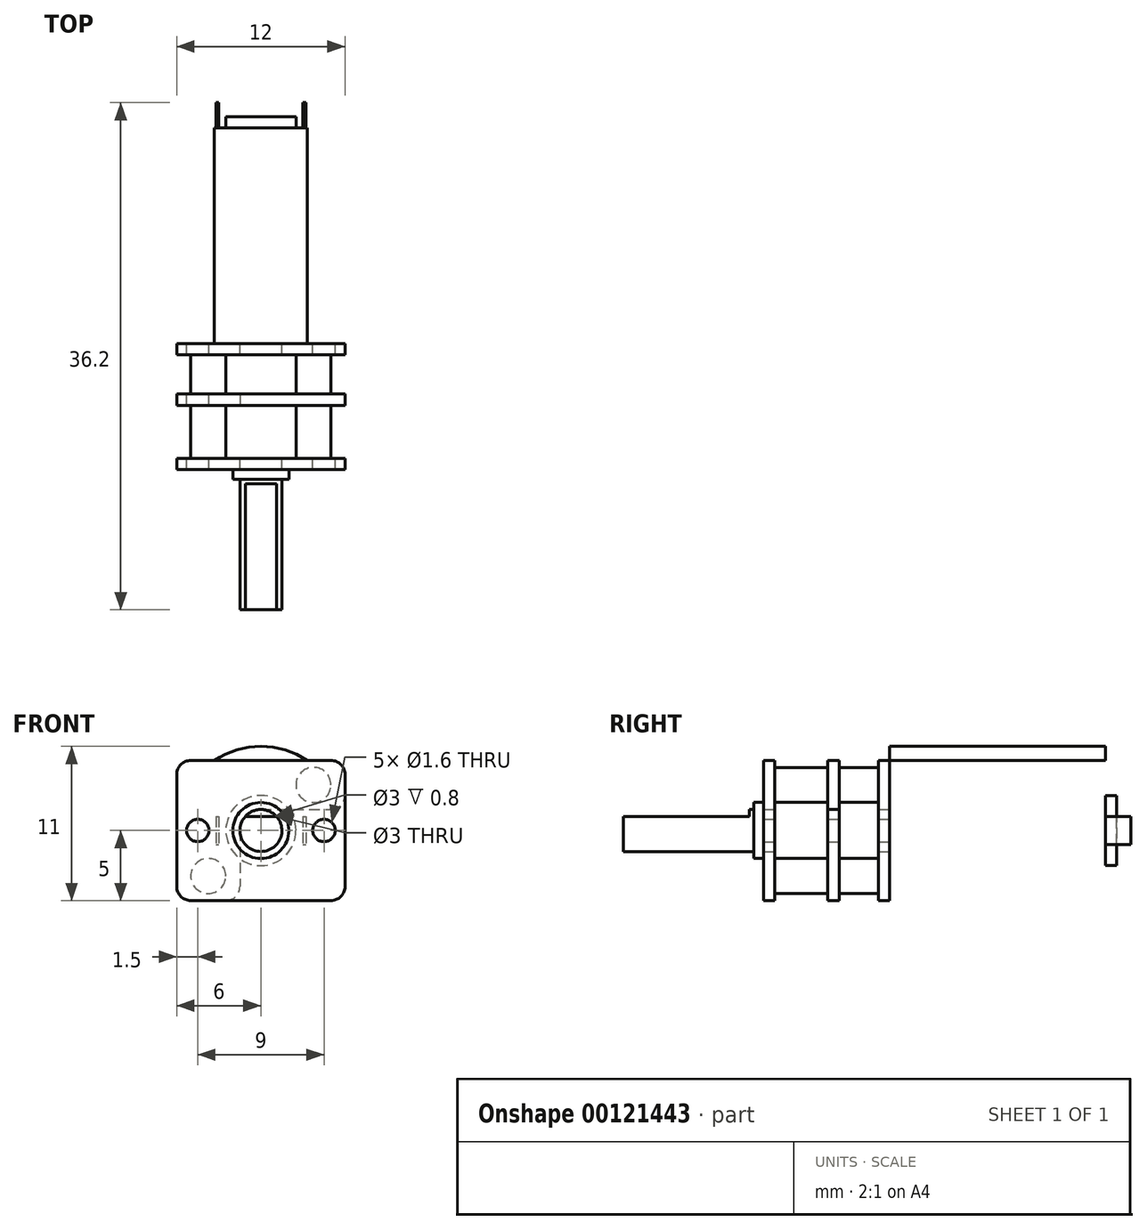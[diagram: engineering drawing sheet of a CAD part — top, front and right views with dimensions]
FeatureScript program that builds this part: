
annotation { "Feature Type Name" : "Feature", "Feature Type Description" : "" }
export const myFeature = defineFeature(function(context is Context, id is Id, definition is map)
    precondition{}
    {
        {
            var Q0;
            Q0=qCreatedBy(makeId("Front.planeOp"),FACE);
            var sketch = newSketch(context, id + "F0", { "sketchPlane" : qUnion([Q0])});
            skCircle(sketch, "E0", {"center": v(0, 0) * mm, "radius": 6 * mm});
            skLineSegment(sketch, "E1.bottom", {"start": v(-6, -5) * mm, "end": v(6, -5) * mm});
            skLineSegment(sketch, "E1.top", {"start": v(-6, 5) * mm, "end": v(6, 5) * mm});
            skLineSegment(sketch, "E1.left", {"start": v(-6, -5) * mm, "end": v(-6, 5) * mm});
            skLineSegment(sketch, "E1.right", {"start": v(6, -5) * mm, "end": v(6, 5) * mm});
            skSolve(sketch);
        }
        {
            var Q0;
            {var subQ0=sQuery(id+"F0.wireOp",EDGE,"E0");var subQ6=sQuery(id+"F0.wireOp",EDGE,"E1.top");var subQ7=makeQuery(id+"F0.imprint","INTERSECT",VERTEX,{"disambiguationData":[OD(0.0)],"derivedFrom":[subQ0,subQ6]});Q0=makeQuery(id+"F0.imprint","IMPRINT",FACE,{"disambiguationData":[TD([[makeQuery(id+"F0.imprint","IMPRINT",EDGE,{"disambiguationData":[TD([[subQ7,1.0]])],"derivedFrom":subQ0}),1.0]])]});}
            extrude(context, id + "F1", {"entities" : qUnion([Q0]), "depth" : 15.4 * mm});
        }
        {
            var Q0;
            Q0=qCreatedBy(makeId("Front.planeOp"),FACE);
            var sketch = newSketch(context, id + "F2", { "sketchPlane" : qUnion([Q0])});
            skLineSegment(sketch, "E2.bottom", {"start": v(-3.2, 1) * mm, "end": v(-3, 1) * mm});
            skLineSegment(sketch, "E2.top", {"start": v(-3.2, -1) * mm, "end": v(-3, -1) * mm});
            skLineSegment(sketch, "E2.left", {"start": v(-3.2, 1) * mm, "end": v(-3.2, -1) * mm});
            skLineSegment(sketch, "E2.right", {"start": v(-3, 1) * mm, "end": v(-3, -1) * mm});
            skLineSegment(sketch, "E3.bottom", {"start": v(3, 1) * mm, "end": v(3.2, 1) * mm});
            skLineSegment(sketch, "E3.top", {"start": v(3, -1) * mm, "end": v(3.2, -1) * mm});
            skLineSegment(sketch, "E3.left", {"start": v(3, 1) * mm, "end": v(3, -1) * mm});
            skLineSegment(sketch, "E3.right", {"start": v(3.2, 1) * mm, "end": v(3.2, -1) * mm});
            skLineSegment(sketch, "E4", {"start": v(-3, 0) * mm, "end": v(3, 0) * mm});
            skCircle(sketch, "E5", {"center": v(0, 0) * mm, "radius": 2.5 * mm});
            skSolve(sketch);
        }
        {
            var Q0;
            {var subQ0=sQuery(id+"F2.wireOp",EDGE,"E5");var subQ1=sQuery(id+"F2.wireOp",EDGE,"E4");var subQ2=makeQuery(id+"F2.imprint","INTERSECT",VERTEX,{"disambiguationData":[OD(0.0)],"derivedFrom":[subQ1,subQ0]});Q0=makeQuery(id+"F2.imprint","IMPRINT",FACE,{"disambiguationData":[TD([[makeQuery(id+"F2.imprint","IMPRINT",EDGE,{"disambiguationData":[TD([[subQ2,-1.0]])],"derivedFrom":subQ1}),-1.0]])]});}
            var Q1;
            {var subQ0=sQuery(id+"F2.wireOp",EDGE,"E5");var subQ1=sQuery(id+"F2.wireOp",EDGE,"E4");var subQ2=makeQuery(id+"F2.imprint","INTERSECT",VERTEX,{"disambiguationData":[OD(0.0)],"derivedFrom":[subQ1,subQ0]});Q1=makeQuery(id+"F2.imprint","IMPRINT",FACE,{"disambiguationData":[TD([[makeQuery(id+"F2.imprint","IMPRINT",EDGE,{"disambiguationData":[TD([[subQ2,-1.0]])],"derivedFrom":subQ1}),1.0]])]});}
            extrude(context, id + "F3", {"entities" : qUnion([Q0, Q1]), "operationType" : NewBodyOperationType.ADD, "oppositeDirection" : true, "depth" : .8 * mm});
        }
        {
            var Q0;
            {var subQ3=sQuery(id+"F2.wireOp",EDGE,"E3.bottom");Q0=makeQuery(id+"F2.imprint","IMPRINT",FACE,{"disambiguationData":[TD([[makeQuery(id+"F2.imprint","IMPRINT",EDGE,{"derivedFrom":subQ3}),-1.0]])]});}
            var Q1;
            {var subQ1=sQuery(id+"F2.wireOp",EDGE,"E2.bottom");Q1=makeQuery(id+"F2.imprint","IMPRINT",FACE,{"disambiguationData":[TD([[makeQuery(id+"F2.imprint","IMPRINT",EDGE,{"derivedFrom":subQ1}),-1.0]])]});}
            extrude(context, id + "F4", {"entities" : qUnion([Q0, Q1]), "operationType" : NewBodyOperationType.ADD, "oppositeDirection" : true, "depth" : 1.8 * mm});
        }
        {
            var Q0;
            Q0=makeQuery(id+"F1.opExtrude","CAP_FACE",FACE,{"disambiguationData":[OSD([sQuery(id+"F0.wireOp",EDGE,"E0"),sQuery(id+"F0.wireOp",EDGE,"E1.bottom"),sQuery(id+"F0.wireOp",EDGE,"E1.top")])],"isStart":false});
            var sketch = newSketch(context, id + "F5", { "sketchPlane" : qUnion([Q0])});
            skLineSegment(sketch, "E6.bottom", {"start": v(-5, 5) * mm, "end": v(5, 5) * mm});
            skLineSegment(sketch, "E6.top", {"start": v(-5, -5) * mm, "end": v(5, -5) * mm});
            skLineSegment(sketch, "E6.left", {"start": v(-6, 4) * mm, "end": v(-6, -4) * mm});
            skLineSegment(sketch, "E6.right", {"start": v(6, 4) * mm, "end": v(6, -4) * mm});
            skPoint(sketch, "E7.visualSharp", {"position": v(-6, 5) * mm});
            skArc(sketch, "E7.filletArc", {"start": v(-5, 5) * mm, "mid": v(-5.7, 4.7) * mm, "end": v(-6, 4) * mm});
            skPoint(sketch, "E8.visualSharp", {"position": v(6, 5) * mm});
            skArc(sketch, "E8.filletArc", {"start": v(6, 4) * mm, "mid": v(5.7, 4.7) * mm, "end": v(5, 5) * mm});
            skPoint(sketch, "E9.visualSharp", {"position": v(6, -5) * mm});
            skArc(sketch, "E9.filletArc", {"start": v(5, -5) * mm, "mid": v(5.7, -4.7) * mm, "end": v(6, -4) * mm});
            skPoint(sketch, "E10.visualSharp", {"position": v(-6, -5) * mm});
            skArc(sketch, "E10.filletArc", {"start": v(-6, -4) * mm, "mid": v(-5.7, -4.7) * mm, "end": v(-5, -5) * mm});
            skCircle(sketch, "E11", {"center": v(-4.5, 0) * mm, "radius": 0.8 * mm});
            skCircle(sketch, "E12", {"center": v(4.5, 0) * mm, "radius": 0.8 * mm});
            skCircle(sketch, "E13", {"center": v(0, 0) * mm, "radius": 1.5 * mm});
            skSolve(sketch);
        }
        {
            var Q0;
            Q0 = qSketchRegion(id + "F5", true);
            extrude(context, id + "F6", {"entities" : qUnion([Q0]), "operationType" : NewBodyOperationType.ADD, "depth" : 9 * mm});
        }
        {
            var Q0;
            Q0=qCreatedBy(makeId("Right.planeOp"),FACE);
            var sketch = newSketch(context, id + "F7", { "sketchPlane" : qUnion([Q0])});
            skLineSegment(sketch, "E14.bottom", {"start": v(-23.6, 5) * mm, "end": v(-19.8, 5) * mm});
            skLineSegment(sketch, "E14.top", {"start": v(-23.6, -5) * mm, "end": v(-19.8, -5) * mm});
            skLineSegment(sketch, "E14.left", {"start": v(-23.6, 5) * mm, "end": v(-23.6, -5) * mm});
            skLineSegment(sketch, "E14.right", {"start": v(-19.8, 5) * mm, "end": v(-19.8, -5) * mm});
            skLineSegment(sketch, "E15.bottom", {"start": v(-19, 5) * mm, "end": v(-16.2, 5) * mm});
            skLineSegment(sketch, "E15.top", {"start": v(-19, -5) * mm, "end": v(-16.2, -5) * mm});
            skLineSegment(sketch, "E15.left", {"start": v(-19, 5) * mm, "end": v(-19, -5) * mm});
            skLineSegment(sketch, "E15.right", {"start": v(-16.2, 5) * mm, "end": v(-16.2, -5) * mm});
            skSolve(sketch);
        }
        {
            var Q0;
            Q0 = qSketchRegion(id + "F7", true);
            extrude(context, id + "F8", {"entities" : qUnion([Q0]), "operationType" : NewBodyOperationType.REMOVE, "oppositeDirection" : true, "depth" : 25 * mm, "hasSecondDirection" : true, "secondDirectionOppositeDirection" : false, "secondDirectionDepth" : 25 * mm});
        }
        {
            var Q0;
            Q0=makeQuery(id+"F8.boolean.opBoolean","COPY",FACE,{"derivedFrom":makeQuery(id+"F8.opExtrude","SWEPT_FACE",FACE,{"disambiguationData":[OSD([sQuery(id+"F7.wireOp",EDGE,"E14.right")])]})});
            var sketch = newSketch(context, id + "F9", { "sketchPlane" : qUnion([Q0])});
            skPoint(sketch, "E16.visualSharp", {"position": v(6, 0) * mm});
            skPoint(sketch, "E17.visualSharp", {"position": v(0, -5) * mm});
            skLineSegment(sketch, "E18", {"start": v(0, 1.5) * mm, "end": v(5, 1.5) * mm});
            skLineSegment(sketch, "E19", {"start": v(-1.5, 0) * mm, "end": v(-1.5, -4) * mm});
            skLineSegment(sketch, "E20", {"start": v(-1.5, -6) * mm, "end": v(7, -6) * mm});
            skArc(sketch, "E21", {"start": v(0, 1.5) * mm, "mid": v(-1.06, 1.06) * mm, "end": v(-1.5, 0) * mm});
            skLineSegment(sketch, "E22", {"start": v(6, 2.5) * mm, "end": v(6, 2.5) * mm});
            skLineSegment(sketch, "E23", {"start": v(6, 2.5) * mm, "end": v(7, 2.5) * mm});
            skLineSegment(sketch, "E24", {"start": v(-2.5, -5) * mm, "end": v(-2.5, -5) * mm});
            skLineSegment(sketch, "E25", {"start": v(-2.5, -5) * mm, "end": v(-2.5, -6) * mm});
            skLineSegment(sketch, "E26", {"start": v(-2.5, -6) * mm, "end": v(-1.5, -6) * mm});
            skLineSegment(sketch, "E27", {"start": v(7, 2.5) * mm, "end": v(7, -6) * mm});
            skPoint(sketch, "E28.visualSharp", {"position": v(6, 1.5) * mm});
            skArc(sketch, "E28.filletArc", {"start": v(5, 1.5) * mm, "mid": v(5.7, 1.8) * mm, "end": v(6, 2.5) * mm});
            skPoint(sketch, "E29.visualSharp", {"position": v(-1.5, -5) * mm});
            skArc(sketch, "E29.filletArc", {"start": v(-2.5, -5) * mm, "mid": v(-1.8, -4.7) * mm, "end": v(-1.5, -4) * mm});
            skSolve(sketch);
        }
        {
            var Q0;
            Q0 = qSketchRegion(id + "F9", true);
            extrude(context, id + "F10", {"entities" : qUnion([Q0]), "operationType" : NewBodyOperationType.REMOVE, "oppositeDirection" : true, "depth" : 1 * mm});
        }
        {
            var Q0;
            Q0=makeQuery(id+"F8.boolean.opBoolean","COPY",FACE,{"derivedFrom":makeQuery(id+"F8.opExtrude","SWEPT_FACE",FACE,{"disambiguationData":[OSD([sQuery(id+"F7.wireOp",EDGE,"E15.right")])]})});
            cPlane(context, id + "F11", {"entities" : qUnion([Q0]), "cplaneType" : CPlaneType.OFFSET, "offset" : 0 * mm, "width" : 150 * mm, "height" : 150 * mm});
        }
        {
            var Q0;
            Q0=qCreatedBy(id+"F11.planeOp",FACE);
            var sketch = newSketch(context, id + "F12", { "sketchPlane" : qUnion([Q0])});
            skCircle(sketch, "E30", {"center": v(-3.75, -3.25) * mm, "radius": 1.25 * mm});
            skCircle(sketch, "E31", {"center": v(3.75, 3.25) * mm, "radius": 1.25 * mm});
            skSolve(sketch);
        }
        {
            var Q0;
            Q0 = qSketchRegion(id + "F12", true);
            extrude(context, id + "F13", {"entities" : qUnion([Q0]), "operationType" : NewBodyOperationType.ADD, "depth" : 7.4 * mm});
        }
        {
            var Q0;
            Q0=makeQuery(id+"F6.opExtrude","CAP_FACE",FACE,{"disambiguationData":[OSD([sQuery(id+"F5.wireOp",EDGE,"E6.bottom"),sQuery(id+"F5.wireOp",EDGE,"E6.top"),sQuery(id+"F5.wireOp",EDGE,"E6.left"),sQuery(id+"F5.wireOp",EDGE,"E6.right"),sQuery(id+"F5.wireOp",EDGE,"E7.filletArc"),sQuery(id+"F5.wireOp",EDGE,"E8.filletArc"),sQuery(id+"F5.wireOp",EDGE,"E9.filletArc"),sQuery(id+"F5.wireOp",EDGE,"E10.filletArc"),sQuery(id+"F5.wireOp",EDGE,"E11"),sQuery(id+"F5.wireOp",EDGE,"E12"),sQuery(id+"F5.wireOp",EDGE,"E13")])],"isStart":false});
            cPlane(context, id + "F14", {"entities" : qUnion([Q0]), "cplaneType" : CPlaneType.OFFSET, "offset" : 0 * mm, "width" : 150 * mm, "height" : 150 * mm});
        }
        {
            var Q0;
            Q0=qCreatedBy(id+"F14.planeOp",FACE);
            var sketch = newSketch(context, id + "F15", { "sketchPlane" : qUnion([Q0])});
            skCircle(sketch, "E32", {"center": v(0, 0) * mm, "radius": 2 * mm});
            skCircle(sketch, "E33", {"center": v(0, 0) * mm, "radius": 1.5 * mm});
            skLineSegment(sketch, "E34", {"start": v(-1.12, 1) * mm, "end": v(1.12, 1) * mm});
            skSolve(sketch);
        }
        {
            var Q0;
            Q0=makeQuery(id+"F15.imprint","IMPRINT",FACE,{"disambiguationData":[TD([[makeQuery(id+"F15.imprint","IMPRINT",EDGE,{"derivedFrom":sQuery(id+"F15.wireOp",EDGE,"E32")}),1.0]])]});
            extrude(context, id + "F16", {"entities" : qUnion([Q0]), "operationType" : NewBodyOperationType.ADD, "depth" : .7 * mm});
        }
        {
            var Q0;
            {var subQ0=sQuery(id+"F15.wireOp",EDGE,"E34");Q0=makeQuery(id+"F15.imprint","IMPRINT",FACE,{"disambiguationData":[TD([[makeQuery(id+"F15.imprint","IMPRINT",EDGE,{"derivedFrom":subQ0}),1.0]])]});}
            var Q1;
            {var subQ0=sQuery(id+"F15.wireOp",EDGE,"E34");Q1=makeQuery(id+"F15.imprint","IMPRINT",FACE,{"disambiguationData":[TD([[makeQuery(id+"F15.imprint","IMPRINT",EDGE,{"derivedFrom":subQ0}),-1.0]])]});}
            extrude(context, id + "F17", {"entities" : qUnion([Q0, Q1]), "operationType" : NewBodyOperationType.ADD, "depth" : 1 * mm});
        }
        {
            var Q0;
            {var subQ0=sQuery(id+"F15.wireOp",EDGE,"E34");Q0=makeQuery(id+"F15.imprint","IMPRINT",FACE,{"disambiguationData":[TD([[makeQuery(id+"F15.imprint","IMPRINT",EDGE,{"derivedFrom":subQ0}),-1.0]])]});}
            extrude(context, id + "F18", {"entities" : qUnion([Q0]), "operationType" : NewBodyOperationType.ADD, "depth" : 10 * mm});
        }
    });
